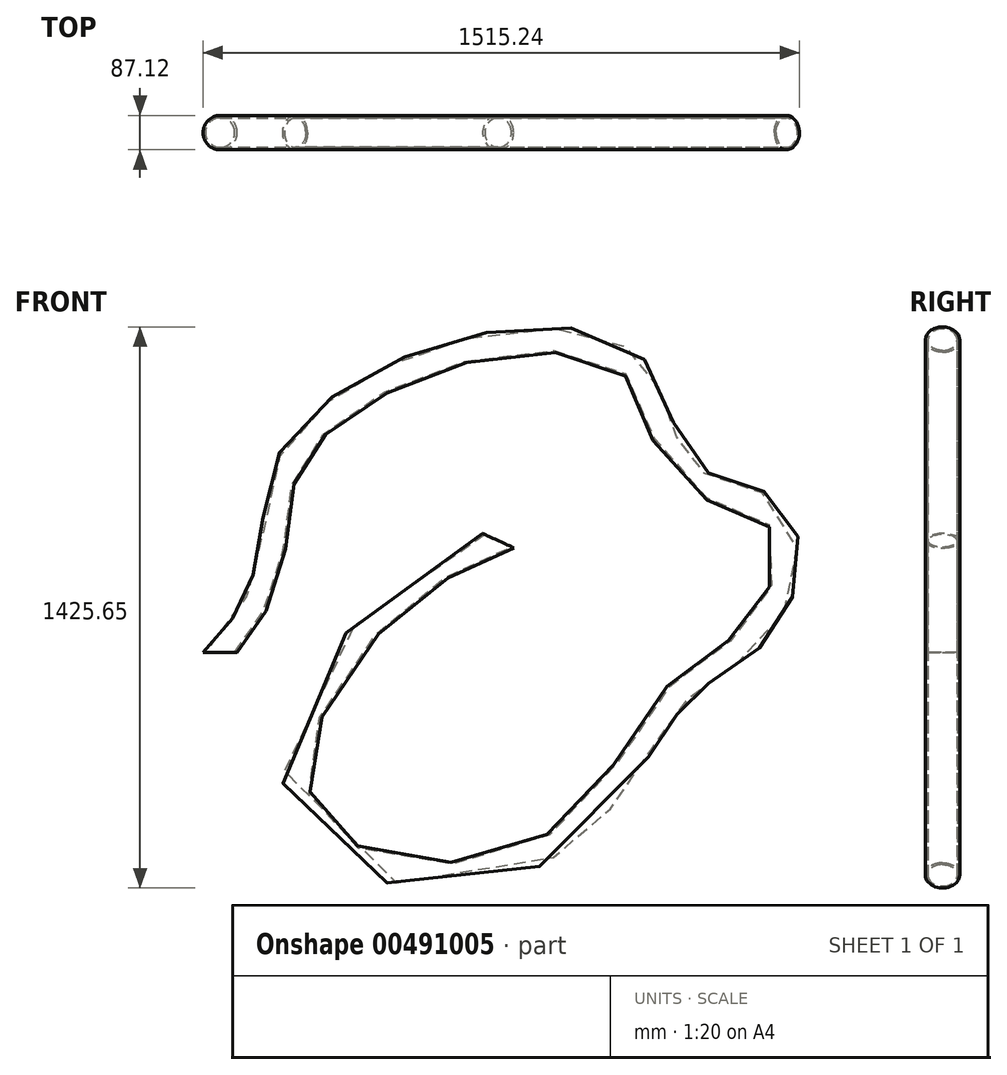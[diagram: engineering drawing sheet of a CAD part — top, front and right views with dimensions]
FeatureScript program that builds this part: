
annotation { "Feature Type Name" : "Feature", "Feature Type Description" : "" }
export const myFeature = defineFeature(function(context is Context, id is Id, definition is map)
    precondition{}
    {
        {
            var Q0;
            Q0=qCreatedBy(makeId("Top.planeOp"),FACE);
            var sketch = newSketch(context, id + "F0", { "sketchPlane" : qUnion([Q0])});
            skCircle(sketch, "E0", {"center": v(0, 0) * mm, "radius": 43.56 * mm});
            skCircle(sketch, "E1", {"center": v(0, 0) * mm, "radius": 37.2 * mm});
            skSolve(sketch);
        }
        {
            var Q0;
            Q0=qCreatedBy(makeId("Front.planeOp"),FACE);
            var sketch = newSketch(context, id + "F1", { "sketchPlane" : qUnion([Q0])});
            skFitSpline(sketch, "E2", {"points": [v(0, 0) * mm, v(69.37, 88.38) * mm, v(132.32, 263.42) * mm, v(169.77, 470.19) * mm, v(355.37, 657.41) * mm, v(731.85, 787.57) * mm, v(1056.5, 716.2) * mm, v(1185.43, 453.71) * mm, v(1406.47, 347.8) * mm, v(1390.35, 83.02) * mm, v(1171.62, -96.57) * mm, v(882.2, -465.28) * mm, v(374.24, -536.91) * mm, v(191.9, -295.96) * mm, v(439.37, 127.34) * mm, v(706.37, 283.64) * mm], "startDerivative": vector(1761.67, 1926.06) * mm, "endDerivative": vector(3866.66, 1628.57) * mm});
            skSolve(sketch);
        }
        {
            var Q0;
            Q0=makeQuery(id+"F0.imprint","IMPRINT",FACE,{"disambiguationData":[TD([[makeQuery(id+"F0.imprint","IMPRINT",EDGE,{"derivedFrom":sQuery(id+"F0.wireOp",EDGE,"E0")}),1.0]])]});
            var Q1;
            Q1=sQuery(id+"F1.wireOp",EDGE,"E2");
            sweep(context, id + "F2", {"profiles" : qUnion([Q0]), "path" : qUnion([Q1])});
        }
    });
